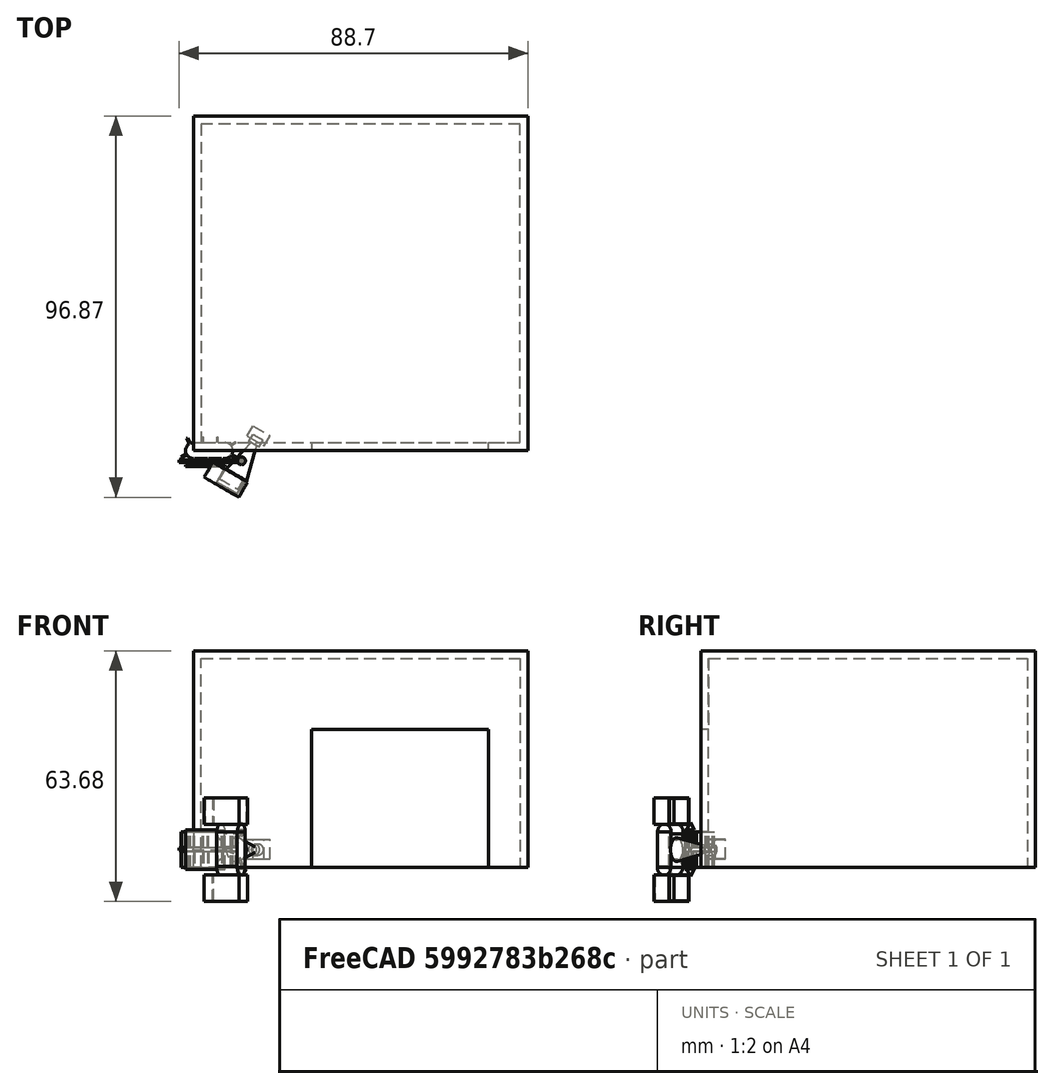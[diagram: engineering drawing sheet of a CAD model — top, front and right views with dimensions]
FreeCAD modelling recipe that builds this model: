
FCSTD DOCUMENT  (FreeCAD 0.17R13541 (Git))
Label: cruiserbot
License: All rights reserved
LicenseURL: http://en.wikipedia.org/wiki/All_rights_reserved
objects: Part::Box×23, Part::Cylinder×8, Part::MultiFuse×8, Part::Feature×4, Part::Cone×3, Part::Torus×2, Part::FeaturePython×2, Mesh::Feature×1, Part::Mirroring×1
note: 51 computed .brp shape members not serialized (recipe doc carries the construction recipe); baked Part::Feature solids carry a one-line shape summary decoded from their .brp

FEATURE [Part::Cylinder] Cylinder
  Angle = 360
  AttacherType = Attacher::AttachEngine3D
  Height = 4
  Radius = 2
FEATURE [Part::Box] Box  label="Cube"
  AttacherType = Attacher::AttachEngine3D
  Height = 4
  Length = 8
  Placement = pos=(0,-2,0) rot=(0,0,1;0rad)
  Width = 4
FEATURE [Part::Cylinder] Cylinder001
  Angle = 360
  AttacherType = Attacher::AttachEngine3D
  Height = 4
  Placement = pos=(8,0,0) rot=(0,0,1;0rad)
  Radius = 2
FEATURE [Part::MultiFuse] Fusion
  Shapes = -> [Cylinder,Box,Cylinder001]
FEATURE [Part::Box] Box001  label="Cube001"
  AttacherType = Attacher::AttachEngine3D
  Height = 4
  Length = 0.3
  Placement = pos=(0,0,0) rot=(0,0,1;0.523599rad)
  Width = 3.5
FEATURE [Part::Box] Box002  label="Cube002"
  AttacherType = Attacher::AttachEngine3D
  Height = 4
  Length = 0.3
  Placement = pos=(6,0,0) rot=(0,0,1;0rad)
  Width = 3.5
FEATURE [Part::Box] Box003  label="Cube003"
  AttacherType = Attacher::AttachEngine3D
  Height = 4
  Length = 0.3
  Placement = pos=(7.7321,-3,0) rot=(0,0,1;0.523599rad)
  Width = 3.5
FEATURE [Part::Box] Box004  label="Cube004"
  AttacherType = Attacher::AttachEngine3D
  Height = 4
  Length = 0.3
  Placement = pos=(0,-3.5,0) rot=(0,0,1;0rad)
  Width = 3.5
FEATURE [Part::Box] Box010  label="Cube010"
  AttacherType = Attacher::AttachEngine3D
  Height = 10
  Length = 10
  Placement = pos=(-2,-4,-0.5) rot=(0,0,1;0rad)
  Width = 0.3
FEATURE [Part::Cylinder] Cylinder006
  Angle = 360
  AttacherType = Attacher::AttachEngine3D
  Height = 6
  Placement = pos=(12.1026,-9.31647,-1.25483e-06) rot=(-0.250563,-0.935113,-0.250563;1.63783rad)
  Radius = 2
FEATURE [Part::Cylinder] Cylinder007
  Angle = 360
  AttacherType = Attacher::AttachEngine3D
  Height = 6
  Placement = pos=(12.1526,-9.22986,9) rot=(-0.250563,-0.935113,-0.250563;1.63783rad)
  Radius = 2
FEATURE [Part::Box] Box012  label="Cube012"
  AttacherType = Attacher::AttachEngine3D
  Height = 9
  Length = 6
  Placement = pos=(5.9155,-8.0341,0) rot=(0,0,-1;0.523599rad)
  Width = 4
FEATURE [Part::Cylinder] Cylinder008
  Angle = 360
  AttacherType = Attacher::AttachEngine3D
  Height = 11
  Placement = pos=(7.3,-2.7,7) rot=(0,-1,0;1.5708rad)
  Radius = 0.3
FEATURE [Part::Torus] Torus
  Angle1 = -180
  Angle2 = 180
  Angle3 = 90
  AttacherType = Attacher::AttachEngine3D
  Placement = pos=(7.3,-2.7,12) rot=(-1,0,0;1.5708rad)
  Radius1 = 5
  Radius2 = 0.3
FEATURE [Part::Torus] Torus001
  Angle1 = -180
  Angle2 = 180
  Angle3 = 90
  AttacherType = Attacher::AttachEngine3D
  Placement = pos=(7.3,-2.7,2) rot=(0.57735,0.57735,0.57735;4.18879rad)
  Radius1 = 5
  Radius2 = 0.3
FEATURE [Part::Cone] Cone
  Angle = 360
  AttacherType = Attacher::AttachEngine3D
  Height = 2
  Placement = pos=(12.3,-2.6,0) rot=(0,0,1;0rad)
  Radius1 = 0
  Radius2 = 1
FEATURE [Part::Cone] Cone001
  Angle = 360
  AttacherType = Attacher::AttachEngine3D
  Height = 2
  Placement = pos=(12.2,-2.6,11.8) rot=(0,0,1;0rad)
  Radius1 = 1
  Radius2 = 0
FEATURE [Part::Box] Box013  label="Cube013"
  AttacherType = Attacher::AttachEngine3D
  Height = 5
  Length = 5
  Placement = pos=(13.6603,3.66025,2.1) rot=(0,0,-1;0.523599rad)
  Width = 3
FEATURE [Part::Cylinder] Cylinder009
  Angle = 360
  AttacherType = Attacher::AttachEngine3D
  Height = 2
  Placement = pos=(15.3753,1.63083,4.5) rot=(-0.935113,0.250563,-0.250563;1.63783rad)
  Radius = 1.5
FEATURE [Part::Box] Box014  label="Cube014"
  AttacherType = Attacher::AttachEngine3D
  Height = 4
  Length = 0.3
  Placement = pos=(2.3,0,0) rot=(0,0,1;0rad)
  Width = 3.5
FEATURE [Part::Box] Box015  label="Cube015"
  AttacherType = Attacher::AttachEngine3D
  Height = 4
  Length = 0.3
  Placement = pos=(3.6,-3.5,0) rot=(0,0,1;0rad)
  Width = 3.5
FEATURE [Part::Box] Box016  label="Cube016"
  AttacherType = Attacher::AttachEngine3D
  Height = 4
  Length = 0.3
  Placement = pos=(-0.00442784,-0.104039,0) rot=(0,0,1;2.0944rad)
  Width = 3.5
FEATURE [Part::Box] Box017  label="Cube017"
  AttacherType = Attacher::AttachEngine3D
  Height = 4
  Length = 0.3
  Placement = pos=(10.8522,1.89167,0) rot=(0,0,1;2.0944rad)
  Width = 3.5
FEATURE [Part::Box] Box018  label="Cube018"
  AttacherType = Attacher::AttachEngine3D
  Height = 4
  Length = 0.3
  Placement = pos=(7.89291,0.0153577,0) rot=(0,0,-1;2.0944rad)
  Width = 3.5
FEATURE [Part::MultiFuse] Fusion008
  Shapes = -> [Box004,Box018,Box017,Box016,Box014,Box003,Box001,Box002,Box015]
FEATURE [Part::Box] Box019  label="Cube019"
  AttacherType = Attacher::AttachEngine3D
  Height = 4
  Length = 0.3
  Placement = pos=(7.89291,0.0153577,0) rot=(0,0,1;4.18879rad)
  Width = 3.5
FEATURE [Part::Cylinder] Cylinder010
  Angle = 360
  AttacherType = Attacher::AttachEngine3D
  Height = 4
  Radius = 2
FEATURE [Part::Box] Box020  label="Cube020"
  AttacherType = Attacher::AttachEngine3D
  Height = 4
  Length = 0.3
  Placement = pos=(10.8522,1.89167,0) rot=(0,0,1;2.0944rad)
  Width = 3.5
FEATURE [Part::Box] Box021  label="Cube021"
  AttacherType = Attacher::AttachEngine3D
  Height = 4
  Length = 0.3
  Placement = pos=(-0.00442784,-0.104039,0) rot=(0,0,1;2.0944rad)
  Width = 3.5
FEATURE [Part::Box] Box022  label="Cube022"
  AttacherType = Attacher::AttachEngine3D
  Height = 4
  Length = 0.3
  Placement = pos=(2.3,0,0) rot=(0,0,1;0rad)
  Width = 3.5
FEATURE [Part::Box] Box023  label="Cube023"
  AttacherType = Attacher::AttachEngine3D
  Height = 4
  Length = 0.3
  Placement = pos=(7.7321,-3,0) rot=(0,0,1;0.523599rad)
  Width = 3.5
FEATURE [Part::Box] Box024  label="Cube024"
  AttacherType = Attacher::AttachEngine3D
  Height = 4
  Length = 0.3
  Placement = pos=(0,0,0) rot=(0,0,1;0.523599rad)
  Width = 3.5
FEATURE [Part::Cylinder] Cylinder011
  Angle = 360
  AttacherType = Attacher::AttachEngine3D
  Height = 4
  Placement = pos=(8,0,0) rot=(0,0,1;0rad)
  Radius = 2
FEATURE [Part::Box] Box025  label="Cube025"
  AttacherType = Attacher::AttachEngine3D
  Height = 4
  Length = 0.3
  Placement = pos=(6,0,0) rot=(0,0,1;0rad)
  Width = 3.5
FEATURE [Part::Box] Box026  label="Cube026"
  AttacherType = Attacher::AttachEngine3D
  Height = 4
  Length = 0.3
  Placement = pos=(0,-3.5,0) rot=(0,0,1;0rad)
  Width = 3.5
FEATURE [Part::Box] Box027  label="Cube027"
  AttacherType = Attacher::AttachEngine3D
  Height = 4
  Length = 0.3
  Placement = pos=(3.6,-3.5,0) rot=(0,0,1;0rad)
  Width = 3.5
FEATURE [Part::MultiFuse] Fusion009
  Placement = pos=(0,0,5) rot=(0,0,1;0rad)
  Shapes = -> [Box026,Box019,Box020,Box021,Box022,Box023,Box024,Box025,Box027]
FEATURE [Part::Box] Box028  label="Cube028"
  AttacherType = Attacher::AttachEngine3D
  Height = 4
  Length = 8
  Placement = pos=(0,-2,0) rot=(0,0,1;0rad)
  Width = 4
FEATURE [Part::MultiFuse] Fusion010
  Placement = pos=(0,0,5) rot=(0,0,1;0rad)
  Shapes = -> [Cylinder010,Box028,Cylinder011]
FEATURE [Part::Cone] Cone002
  Angle = 360
  AttacherType = Attacher::AttachEngine3D
  Height = 9
  Placement = pos=(15.3753,1.63083,4.5) rot=(0.935113,-0.250563,-0.250563;1.63783rad)
  Radius1 = 0.8
  Radius2 = 3
FEATURE [Part::MultiFuse] Fusion011
  Shapes = -> [Box012,Cylinder006,Cylinder007]
FEATURE [Part::MultiFuse] Fusion012
  Placement = pos=(0,0,-2.36) rot=(0,0,1;0rad)
  Shapes = -> [Cylinder008,Torus,Cone001,Cone,Torus001]
FEATURE [Part::MultiFuse] Fusion013
  Shapes = -> [Fusion009,Fusion010]
FEATURE [Part::MultiFuse] Fusion014
  Shapes = -> [Fusion,Fusion008]
FEATURE [Mesh::Feature] bin_2_  label="bin(2)"
FEATURE [Part::Feature] bin_2_001
  shape: bbox 85 x 85 x 55 mm, 44 faces, 0 solids (baked)
FEATURE [Part::Feature] bin_2_001_solid  label="bin_2_001 (Solid)"
  shape: bbox 85 x 85 x 55 mm, 44 faces (baked)
FEATURE [Part::Feature] bin_2_001_solid001  label="bin_2_001 (Solid)001"
  shape: bbox 85 x 85 x 55 mm, 14 faces (baked)
FEATURE [Part::FeaturePython] Scale  # Draft clone (typed FeaturePython)
  Fuse = false
  Objects = -> [bin_2_001_solid001]
  Placement = pos=(4.89867,-2.95526,10.87) rot=(0.935113,-0.250563,-0.250563;1.63783rad)
  Scale = (0.12,0.08,0.08)
FEATURE [Part::Feature] bin_2_001_solid002  label="bin_2_001 (Solid)002"
  shape: bbox 85 x 85 x 55 mm, 14 faces (baked)
FEATURE [Part::FeaturePython] Scale001  # Draft clone (typed FeaturePython)
  Fuse = false
  Objects = -> [bin_2_001_solid002]
  Placement = pos=(4.89867,-2.95526,10.87) rot=(0.935113,-0.250563,-0.250563;1.63783rad)
  Scale = (0.12,0.08,0.08)
FEATURE [Part::Mirroring] Part__Mirroring  label="Scale001 (Mirror #1)"
  Base = (0,0,0)
  Normal = (0,0,1)
  Placement = pos=(0,0,8.99) rot=(0,0,1;0rad)
  Source = -> Scale001
